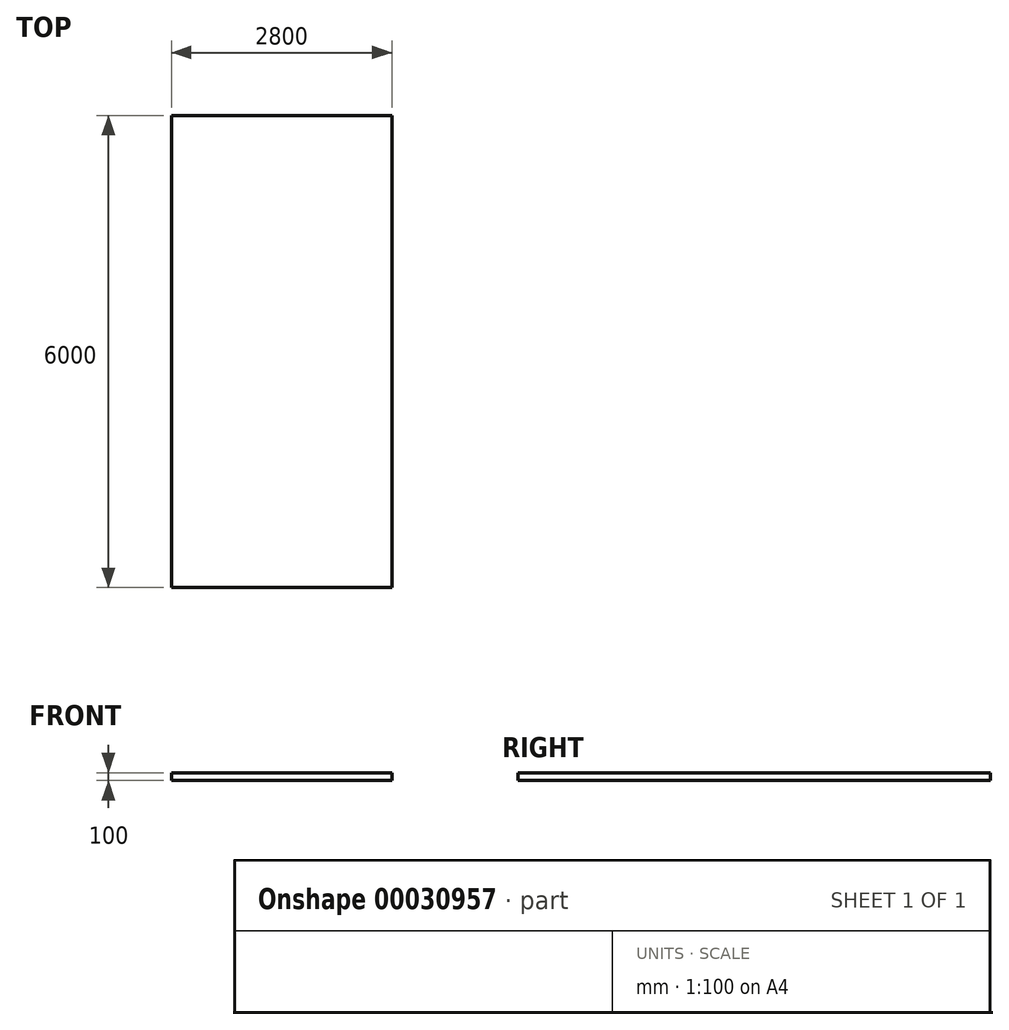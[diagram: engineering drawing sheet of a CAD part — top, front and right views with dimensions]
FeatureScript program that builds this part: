
annotation { "Feature Type Name" : "Feature", "Feature Type Description" : "" }
export const myFeature = defineFeature(function(context is Context, id is Id, definition is map)
    precondition{}
    {
        {
            var Q0;
            Q0=qCreatedBy(makeId("Top.planeOp"),FACE);
            var sketch = newSketch(context, id + "F0", { "sketchPlane" : qUnion([Q0])});
            skLineSegment(sketch, "E0.bottom", {"start": v(0, 0) * mm, "end": v(-2800, 0) * mm});
            skLineSegment(sketch, "E0.top", {"start": v(0, 6000) * mm, "end": v(-2800, 6000) * mm});
            skLineSegment(sketch, "E0.left", {"start": v(0, 0) * mm, "end": v(0, 6000) * mm});
            skLineSegment(sketch, "E0.right", {"start": v(-2800, 0) * mm, "end": v(-2800, 6000) * mm});
            skSolve(sketch);
        }
        {
            var Q0;
            Q0 = qSketchRegion(id + "F0", true);
            extrude(context, id + "F1", {"entities" : qUnion([Q0]), "depth" : 100 * mm});
        }
    });
